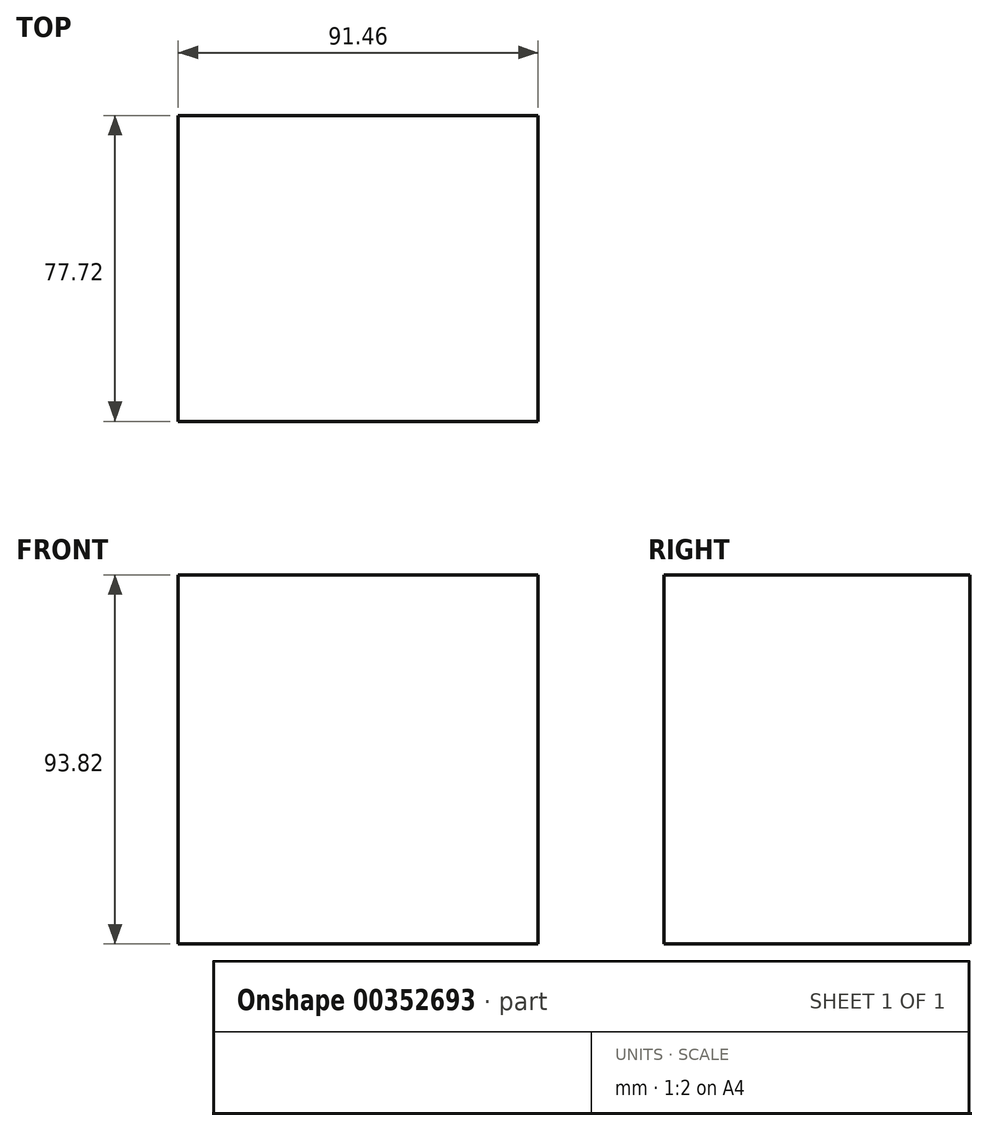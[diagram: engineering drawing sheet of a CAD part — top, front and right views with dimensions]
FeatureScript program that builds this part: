
annotation { "Feature Type Name" : "Feature", "Feature Type Description" : "" }
export const myFeature = defineFeature(function(context is Context, id is Id, definition is map)
    precondition{}
    {
        {
            var Q0;
            Q0=qCreatedBy(makeId("Front.planeOp"),FACE);
            var sketch = newSketch(context, id + "F0", { "sketchPlane" : qUnion([Q0])});
            skLineSegment(sketch, "E0.bottom", {"start": v(-61.23, 57.2) * mm, "end": v(30.23, 57.2) * mm});
            skLineSegment(sketch, "E0.top", {"start": v(-61.23, -36.62) * mm, "end": v(30.23, -36.62) * mm});
            skLineSegment(sketch, "E0.left", {"start": v(-61.23, 57.2) * mm, "end": v(-61.23, -36.62) * mm});
            skLineSegment(sketch, "E0.right", {"start": v(30.23, 57.2) * mm, "end": v(30.23, -36.62) * mm});
            skSolve(sketch);
        }
        {
            var Q0;
            Q0=makeQuery(id+"F0.imprint","IMPRINT",FACE,{"disambiguationData":[TD([[makeQuery(id+"F0.imprint","IMPRINT",EDGE,{"derivedFrom":sQuery(id+"F0.wireOp",EDGE,"E0.bottom")}),-1.0]])]});
            extrude(context, id + "F1", {"entities" : qUnion([Q0]), "depth" : 77.72 * mm});
        }
    });
